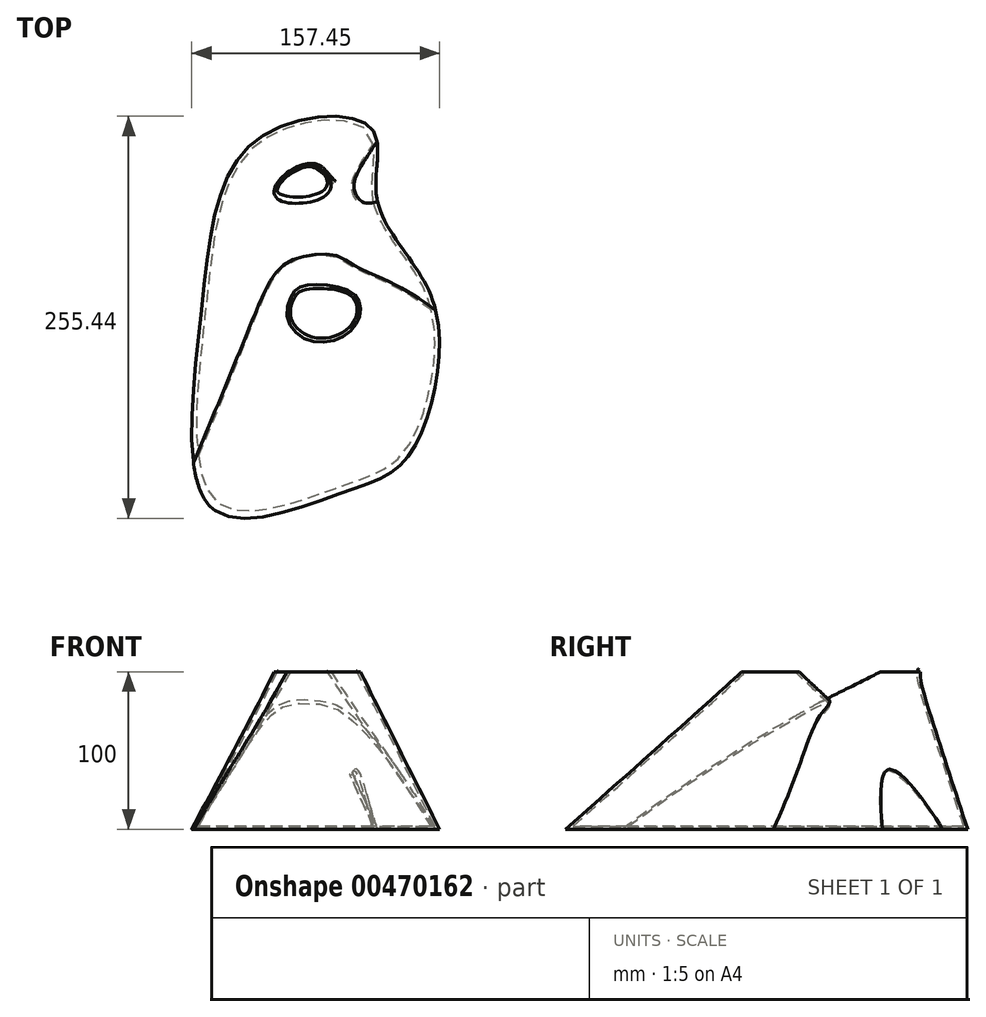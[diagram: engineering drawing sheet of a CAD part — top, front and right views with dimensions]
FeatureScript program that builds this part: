
annotation { "Feature Type Name" : "Feature", "Feature Type Description" : "" }
export const myFeature = defineFeature(function(context is Context, id is Id, definition is map)
    precondition{}
    {
        {
            var Q0;
            Q0=qCreatedBy(makeId("Top.planeOp"),FACE);
            var sketch = newSketch(context, id + "F0", { "sketchPlane" : qUnion([Q0])});
            skLineSegment(sketch, "E0.bottom", {"start": v(-90, 140) * mm, "end": v(90, 140) * mm});
            skLineSegment(sketch, "E0.top", {"start": v(-90, -140) * mm, "end": v(90, -140) * mm});
            skLineSegment(sketch, "E0.left", {"start": v(-90, 140) * mm, "end": v(-90, -140) * mm});
            skLineSegment(sketch, "E0.right", {"start": v(90, 140) * mm, "end": v(90, -140) * mm});
            skPoint(sketch, "E0.middle", {"position": v(0, 0) * mm});
            skFitSpline(sketch, "E1", {"points": [v(-71.54, -121.03) * mm, v(-80.5, 4.3) * mm, v(-43.74, 115.5) * mm, v(27.41, 122.1) * mm, v(31.18, 77.34) * mm, v(63.22, 20.8) * mm, v(68.88, -38.57) * mm, v(48.61, -89.46) * mm, v(9.03, -109.72) * mm, v(-71.54, -121.03) * mm]});
            skSolve(sketch);
        }
        {
            var Q0;
            Q0=qCreatedBy(makeId("Top.planeOp"),FACE);
            cPlane(context, id + "F1", {"entities" : qUnion([Q0]), "cplaneType" : CPlaneType.OFFSET, "offset" : 100 * mm, "width" : 150 * mm, "height" : 150 * mm});
        }
        {
            var Q0;
            Q0=qCreatedBy(id+"F1.planeOp",FACE);
            var sketch = newSketch(context, id + "F2", { "sketchPlane" : qUnion([Q0])});
            skPoint(sketch, "E2.6.internal.orphan", {"position": v(-28.85, 0) * mm});
            skPoint(sketch, "E3.0.internal.orphan", {"position": v(-28.85, 97.45) * mm});
            skPoint(sketch, "E3.4.internal.orphan", {"position": v(0, 65.27) * mm});
            skFitSpline(sketch, "E4", {"points": [v(-31.06, 76.37) * mm, v(-32.57, 86.44) * mm, v(-16.17, 98.56) * mm, v(-2.62, 96.42) * mm, v(0, 80.43) * mm, v(-31.06, 76.37) * mm]});
            skFitSpline(sketch, "E5", {"points": [v(-25.2, 0) * mm, v(-21.4, 17.97) * mm, v(-9.75, 22.49) * mm, v(14.98, 17.73) * mm, v(20.68, 5.6) * mm, v(13.08, -8.18) * mm, v(-9.27, -13.65) * mm, v(-25.2, 0) * mm]});
            skSolve(sketch);
        }
        {
            var Q0;
            Q0=makeQuery(id+"F0.imprint","IMPRINT",FACE,{"disambiguationData":[TD([[makeQuery(id+"F0.imprint","IMPRINT",EDGE,{"derivedFrom":sQuery(id+"F0.wireOp",EDGE,"E1")}),-1.0]])]});
            var Q1;
            Q1=makeQuery(id+"F2.imprint","IMPRINT",FACE,{"disambiguationData":[TD([[makeQuery(id+"F2.imprint","IMPRINT",EDGE,{"derivedFrom":sQuery(id+"F2.wireOp",EDGE,"E5")}),-1.0]])]});
            loft(context, id + "F3", {"sheetProfilesArray" : [{ "sheetProfileEntities" : qUnion([Q0]) }, { "sheetProfileEntities" : qUnion([Q1]) }]});
        }
        {
            var Q1;
            Q1=makeQuery(id+"F0.imprint","IMPRINT",FACE,{"disambiguationData":[TD([[makeQuery(id+"F0.imprint","IMPRINT",EDGE,{"derivedFrom":sQuery(id+"F0.wireOp",EDGE,"E1")}),-1.0]])]});
            var Q2;
            Q2=makeQuery(id+"F2.imprint","IMPRINT",FACE,{"disambiguationData":[TD([[makeQuery(id+"F2.imprint","IMPRINT",EDGE,{"derivedFrom":sQuery(id+"F2.wireOp",EDGE,"E4")}),-1.0]])]});
            loft(context, id + "F4", {"operationType" : NewBodyOperationType.ADD, "sheetProfilesArray" : [{ "sheetProfileEntities" : qUnion([Q1]) }, { "sheetProfileEntities" : qUnion([Q2]) }]});
        }
        {
            var Q0;
            Q0=makeQuery(id+"F4.opLoft","CAP_FACE",FACE,{"disambiguationData":[OSD([makeQuery(id+"F2.imprint","IMPRINT",FACE,{"disambiguationData":[TD([[makeQuery(id+"F2.imprint","IMPRINT",EDGE,{"derivedFrom":sQuery(id+"F2.wireOp",EDGE,"E4")}),-1.0]])]})])],"isStart":true});
            var Q1;
            Q1=makeQuery(id+"F3.opLoft","CAP_FACE",FACE,{"disambiguationData":[OSD([makeQuery(id+"F2.imprint","IMPRINT",FACE,{"disambiguationData":[TD([[makeQuery(id+"F2.imprint","IMPRINT",EDGE,{"derivedFrom":sQuery(id+"F2.wireOp",EDGE,"E5")}),-1.0]])]})])],"isStart":true});
            shell(context, id + "F5", {"entities" : qUnion([Q0, Q1]), "thickness" : 1.8 * mm});
        }
    });
